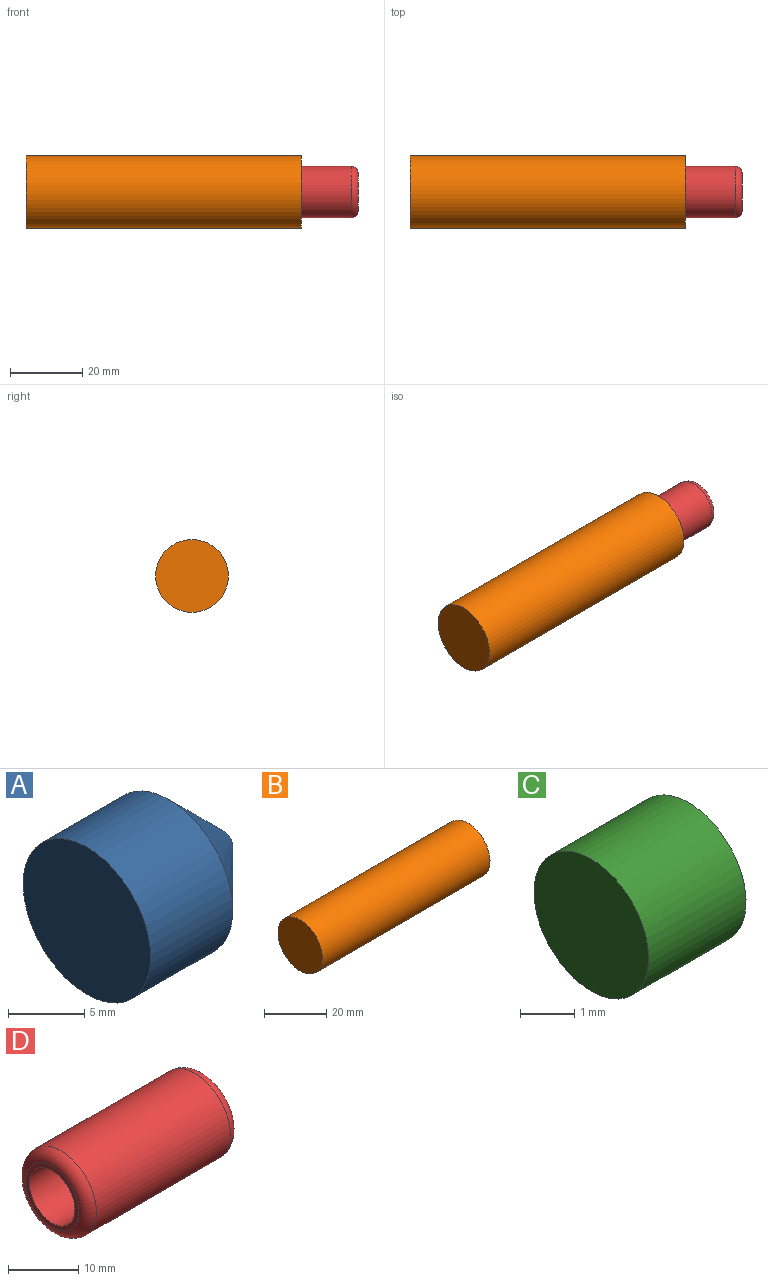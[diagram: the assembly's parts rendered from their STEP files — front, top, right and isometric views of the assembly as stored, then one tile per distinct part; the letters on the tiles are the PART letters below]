
ASSEMBLY  parts=4 mates=3
PART A: 4 faces, bbox 12.7x11.8x11.8 mm
  f0: cylinder r=5.9mm len=11.81mm, axis (-1,0,0), area 282.7mm2, adj f2,f3
  f1: plane 1.65x1.65mm, normal (1,0,0), area 2.1mm2, adj f3
  f2: plane 11.81x11.81mm, normal (-1,0,0), area 109.5mm2, adj f0
  f3: cone r=0.82mm half-angle=45deg, axis (-1,0,0), area 151.8mm2, adj f0,f1
PART B: 3 faces, bbox 76.2x20.1x20.1 mm
  f0: cylinder r=10.06mm len=76.2mm, axis (-1,0,0), area 4818mm2, adj f1,f2
  f1: plane 20.13x20.13mm, normal (1,0,0), area 318.1mm2, adj f0
  f2: plane 20.13x20.13mm, normal (-1,0,0), area 318.1mm2, adj f0
PART C: 3 faces, bbox 2.5x3x3 mm
  f0: cylinder r=1.49mm len=2.98mm, axis (-1,0,0), area 23.8mm2, adj f1,f2
  f1: plane 2.98x2.98mm, normal (1,0,0), area 7mm2, adj f0
  f2: plane 2.98x2.98mm, normal (-1,0,0), area 7mm2, adj f0
PART D: 7 faces, bbox 30.5x15.4x15.4 mm
  f0: cylinder r=7.11mm len=26.92mm, axis (-1,0,0), area 1202.9mm2, adj f3,f4
  f1: plane 10.67x10.67mm, normal (1,0,0), area 89.3mm2, adj f4
  f2: plane 10.67x10.67mm, normal (-1,0,0), area 23.7mm2, adj f3,f5
  f3: torus R=5.33mm, axis (1,0,0), area 113.4mm2, adj f0,f2
  f4: torus R=5.33mm, axis (1,0,0), area 113.4mm2, adj f0,f1
  f5: cylinder r=4.57mm len=27.94mm, axis (-1,0,0), area 802.4mm2, adj f2,f6
  f6: plane 9.14x9.14mm, normal (-1,0,0), area 65.6mm2, adj f5
PLACE A t=(35.26,-31.25,-1.02)mm
PLACE B t=(-40.94,40.25,-6.98)mm
PLACE C t=(45.42,43.13,20.22)mm
PLACE D rot(axis=(1,0,0),0deg) t=(20.51,53.15,-10.99)mm
MATE fastened A.f0 <-> B.f0  axis (-1,0,0) through (35.26,-4.79,46.71)mm
MATE fastened C.f0 <-> A.f0  axis (1,0,0) through (47.96,-4.79,46.71)mm
MATE slider D.f0 <-> C.f0  axis (-1,0,0) through (48.45,-4.79,46.71)mm
